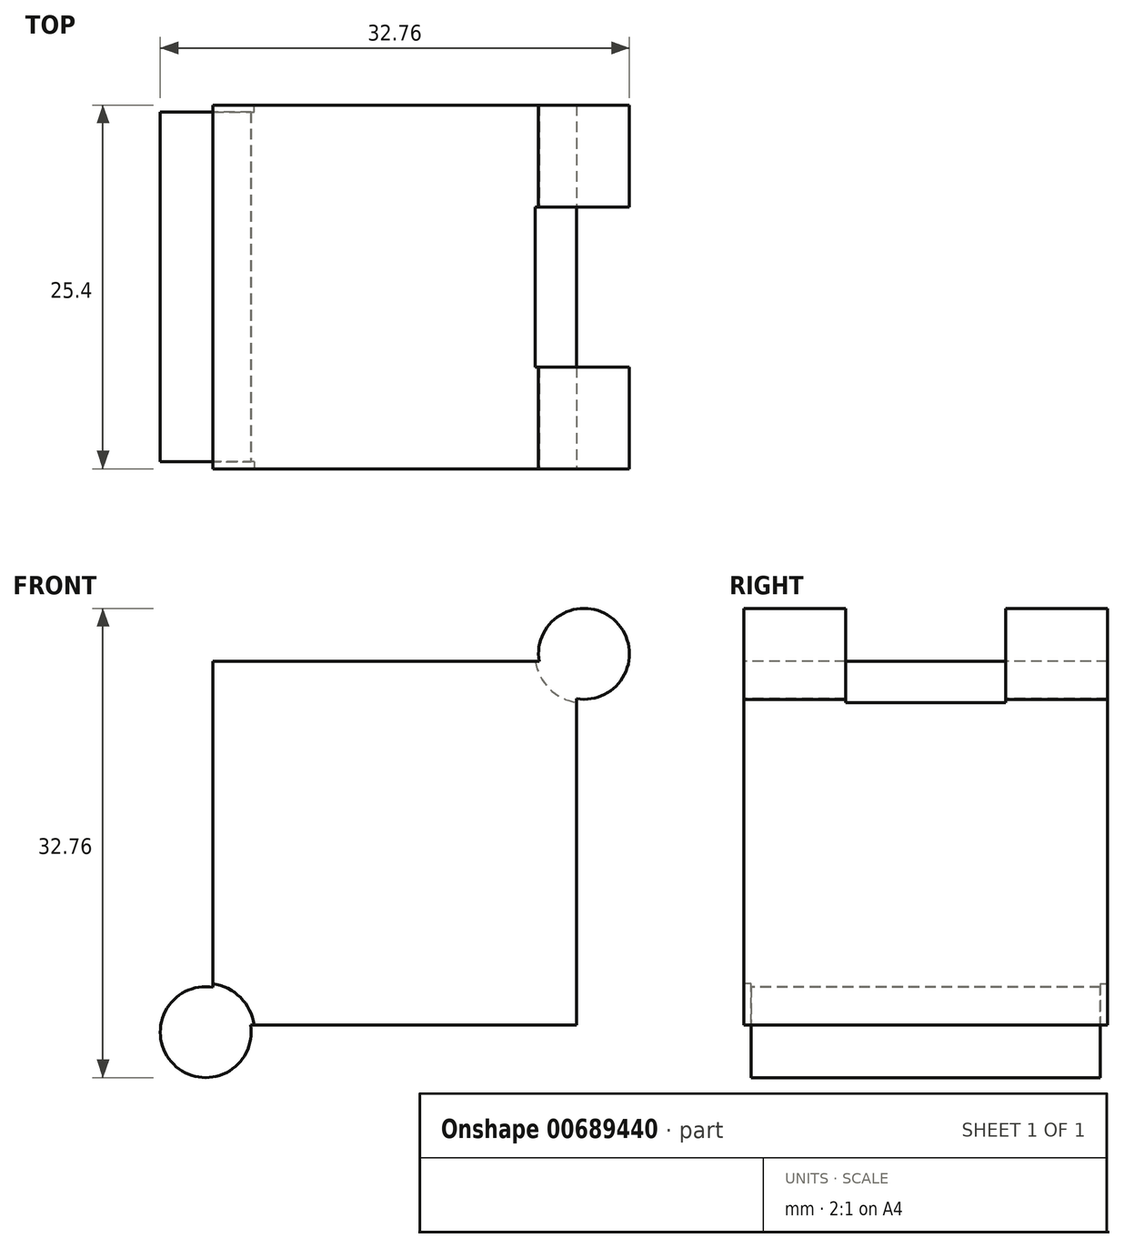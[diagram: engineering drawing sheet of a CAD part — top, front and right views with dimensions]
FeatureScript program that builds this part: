
annotation { "Feature Type Name" : "Feature", "Feature Type Description" : "" }
export const myFeature = defineFeature(function(context is Context, id is Id, definition is map)
    precondition{}
    {
        {
            assignVariable(context, id + "F0", {"name" : "O", "anyValue" : .2});
        }
        {
            var Q0;
            Q0=qCreatedBy(makeId("Front.planeOp"),FACE);
            var sketch = newSketch(context, id + "F1", { "sketchPlane" : qUnion([Q0])});
            skLineSegment(sketch, "E0.bottom", {"start": v(12.7, -12.7) * mm, "end": v(-12.7, -12.7) * mm});
            skLineSegment(sketch, "E0.top", {"start": v(12.7, 12.7) * mm, "end": v(-12.7, 12.7) * mm});
            skLineSegment(sketch, "E0.left", {"start": v(12.7, -12.7) * mm, "end": v(12.7, 12.7) * mm});
            skLineSegment(sketch, "E0.right", {"start": v(-12.7, -12.7) * mm, "end": v(-12.7, 12.7) * mm});
            skPoint(sketch, "E0.middle", {"position": v(0, 0) * mm});
            skSolve(sketch);
        }
        {
            var Q0;
            Q0=makeQuery(id+"F1.imprint","IMPRINT",FACE,{"disambiguationData":[TD([[makeQuery(id+"F1.imprint","IMPRINT",EDGE,{"derivedFrom":sQuery(id+"F1.wireOp",EDGE,"E0.bottom")}),-1.0]])]});
            extrude(context, id + "F2", {"entities" : qUnion([Q0]), "depth" : 25.4 * mm, "offsetDistance" : 25.4 * mm});
        }
        {
            var Q0;
            Q0=makeQuery(id+"F2.opExtrude","CAP_FACE",FACE,{"disambiguationData":[OSD([sQuery(id+"F1.wireOp",EDGE,"E0.bottom"),sQuery(id+"F1.wireOp",EDGE,"E0.top"),sQuery(id+"F1.wireOp",EDGE,"E0.left"),sQuery(id+"F1.wireOp",EDGE,"E0.right")])],"isStart":false});
            var sketch = newSketch(context, id + "F3", { "sketchPlane" : qUnion([Q0])});
            skCircle(sketch, "E1", {"center": v(13.2, 13.2) * mm, "radius": 3.18 * mm});
            skSolve(sketch);
        }
        {
            var Q0;
            {var subQ0=sQuery(id+"F3.wireOp",EDGE,"E1");var subQ1=makeQuery(id+"F2.opExtrude","CAP_EDGE",EDGE,{"disambiguationData":[OSD([sQuery(id+"F1.wireOp",EDGE,"E0.top")])],"isStart":false});var subQ2=makeQuery(id+"F3.imprint","INTERSECT",VERTEX,{"derivedFrom":[subQ1,subQ0]});Q0=makeQuery(id+"F3.imprint","IMPRINT",FACE,{"disambiguationData":[TD([[makeQuery(id+"F3.imprint","IMPRINT",EDGE,{"disambiguationData":[TD([[subQ2,1.0]])],"derivedFrom":subQ0}),1.0]])]});}
            var Q1;
            Q1=makeQuery(id+"F2.opExtrude","CAP_FACE",FACE,{"disambiguationData":[OSD([sQuery(id+"F1.wireOp",EDGE,"E0.bottom"),sQuery(id+"F1.wireOp",EDGE,"E0.top"),sQuery(id+"F1.wireOp",EDGE,"E0.left"),sQuery(id+"F1.wireOp",EDGE,"E0.right")])],"isStart":true});
            extrude(context, id + "F4", {"entities" : qUnion([Q0]), "operationType" : NewBodyOperationType.ADD, "endBound" : BoundingType.UP_TO_SURFACE, "oppositeDirection" : true, "depth" : 25.4 * mm, "endBoundEntityFace" : qUnion([Q1]), "offsetDistance" : 25.4 * mm});
        }
        {
            var Q0;
            {var subQ0=sQuery(id+"F1.wireOp",EDGE,"E0.left");Q0=makeQuery(id+"Fs0qjrKRxYJa69d_1.boolean.opBoolean","MERGE",FACE,{"derivedFrom":[makeQuery(id+"F2.opExtrude","SWEPT_FACE",FACE,{"disambiguationData":[OSD([subQ0])]}),makeQuery(id+"Fs0qjrKRxYJa69d_1.opExtrude","CAP_FACE",FACE,{"disambiguationData":[OSD([subQ0])],"isStart":false})]});}
            var sketch = newSketch(context, id + "F5", { "sketchPlane" : qUnion([Q0])});
            skLineSegment(sketch, "E2.bottom", {"start": v(-7.11, 4.13) * mm, "end": v(-18.29, 4.13) * mm});
            skLineSegment(sketch, "E2.top", {"start": v(-7.11, 21.77) * mm, "end": v(-18.29, 21.77) * mm});
            skLineSegment(sketch, "E2.left", {"start": v(-7.11, 4.13) * mm, "end": v(-7.11, 21.77) * mm});
            skLineSegment(sketch, "E2.right", {"start": v(-18.29, 4.13) * mm, "end": v(-18.29, 21.77) * mm});
            skPoint(sketch, "E2.middle", {"position": v(-12.7, 12.95) * mm});
            skSolve(sketch);
        }
        {
            var Q0;
            {var subQ0=sQuery(id+"F5.wireOp",EDGE,"E2.top");Q0=makeQuery(id+"F5.imprint","IMPRINT",FACE,{"disambiguationData":[TD([[makeQuery(id+"F5.imprint","IMPRINT",EDGE,{"derivedFrom":subQ0}),1.0]])]});}
            var Q1;
            {var subQ0=sQuery(id+"F5.wireOp",EDGE,"E2.bottom");Q1=makeQuery(id+"F5.imprint","IMPRINT",FACE,{"disambiguationData":[TD([[makeQuery(id+"F5.imprint","IMPRINT",EDGE,{"derivedFrom":subQ0}),-1.0]])]});}
            extrude(context, id + "F6", {"entities" : qUnion([Q0, Q1]), "operationType" : NewBodyOperationType.REMOVE, "depth" : 25.4 * mm, "offsetDistance" : 25.4 * mm});
        }
        {
            var Q0;
            Q0=makeQuery(id+"F6.boolean.opBoolean","COPY",FACE,{"derivedFrom":makeQuery(id+"F6.opExtrude","SWEPT_FACE",FACE,{"disambiguationData":[OSD([sQuery(id+"F5.wireOp",EDGE,"E2.left")])]})});
            var sketch = newSketch(context, id + "F7", { "sketchPlane" : qUnion([Q0])});
            skCircle(sketch, "E3", {"center": v(13.2, 13.2) * mm, "radius": 3.43 * mm});
            skSolve(sketch);
        }
        {
            var Q0;
            Q0=makeQuery(id+"F7.imprint","IMPRINT",FACE,{"disambiguationData":[TD([[makeQuery(id+"F7.imprint","IMPRINT",EDGE,{"derivedFrom":sQuery(id+"F7.wireOp",EDGE,"E3")}),1.0]])]});
            var Q1;
            Q1=makeQuery(id+"F6.boolean.opBoolean","COPY",FACE,{"derivedFrom":makeQuery(id+"F6.opExtrude","SWEPT_FACE",FACE,{"disambiguationData":[OSD([sQuery(id+"F5.wireOp",EDGE,"E2.right")])]})});
            extrude(context, id + "F8", {"entities" : qUnion([Q0]), "operationType" : NewBodyOperationType.REMOVE, "endBound" : BoundingType.UP_TO_SURFACE, "depth" : 25.4 * mm, "endBoundEntityFace" : qUnion([Q1]), "offsetDistance" : 25.4 * mm});
        }
        {
            var Q0;
            {var subQ0=sQuery(id+"F1.wireOp",EDGE,"E0.left");var subQ1=sQuery(id+"F1.wireOp",EDGE,"E0.top");Q0=makeQuery(id+"F4.boolean.opBoolean","MERGE",FACE,{"derivedFrom":[makeQuery(id+"F2.opExtrude","CAP_FACE",FACE,{"disambiguationData":[OSD([sQuery(id+"F1.wireOp",EDGE,"E0.bottom"),subQ1,subQ0,sQuery(id+"F1.wireOp",EDGE,"E0.right")])],"isStart":false}),makeQuery(id+"F4.opExtrude","CAP_FACE",FACE,{"disambiguationData":[OSD([subQ1,subQ0,sQuery(id+"F3.wireOp",EDGE,"E1")])],"isStart":true})]});}
            var sketch = newSketch(context, id + "F9", { "sketchPlane" : qUnion([Q0])});
            skCircle(sketch, "E4", {"center": v(-13.2, -13.2) * mm, "radius": 3.18 * mm});
            skSolve(sketch);
        }
        {
            var Q0;
            {var subQ0=sQuery(id+"F9.wireOp",EDGE,"E4");var subQ1=makeQuery(id+"F2.opExtrude","CAP_EDGE",EDGE,{"disambiguationData":[OSD([sQuery(id+"F1.wireOp",EDGE,"E0.bottom")])],"isStart":false});var subQ2=makeQuery(id+"F9.imprint","INTERSECT",VERTEX,{"derivedFrom":[subQ1,subQ0]});Q0=makeQuery(id+"F9.imprint","IMPRINT",FACE,{"disambiguationData":[TD([[makeQuery(id+"F9.imprint","IMPRINT",EDGE,{"disambiguationData":[TD([[subQ2,1.0]])],"derivedFrom":subQ0}),1.0]])]});}
            var Q1;
            {var subQ0=sQuery(id+"F1.wireOp",EDGE,"E0.right");var subQ1=sQuery(id+"F1.wireOp",EDGE,"E0.left");var subQ2=sQuery(id+"F1.wireOp",EDGE,"E0.top");var subQ3=sQuery(id+"F1.wireOp",EDGE,"E0.bottom");Q1=makeQuery(id+"F4.boolean.opBoolean","MERGE",FACE,{"derivedFrom":[makeQuery(id+"F2.opExtrude","CAP_FACE",FACE,{"disambiguationData":[OSD([subQ3,subQ2,subQ1,subQ0])],"isStart":true}),makeQuery(id+"F4.opExtrude","CAP_FACE",FACE,{"disambiguationData":[OSD([subQ3,subQ2,subQ1,subQ0])],"isStart":false})]});}
            extrude(context, id + "F10", {"entities" : qUnion([Q0]), "operationType" : NewBodyOperationType.ADD, "endBound" : BoundingType.UP_TO_SURFACE, "oppositeDirection" : true, "depth" : 25.4 * mm, "endBoundEntityFace" : qUnion([Q1]), "offsetDistance" : 25.4 * mm});
        }
        {
            var Q0;
            {var subQ0=sQuery(id+"F1.wireOp",EDGE,"E0.right");var subQ1=sQuery(id+"F1.wireOp",EDGE,"E0.bottom");var subQ2=sQuery(id+"F1.wireOp",EDGE,"E0.left");var subQ3=sQuery(id+"F1.wireOp",EDGE,"E0.top");Q0=makeQuery(id+"F10.boolean.opBoolean","MERGE",FACE,{"derivedFrom":[makeQuery(id+"F4.boolean.opBoolean","MERGE",FACE,{"derivedFrom":[makeQuery(id+"F2.opExtrude","CAP_FACE",FACE,{"disambiguationData":[OSD([subQ1,subQ3,subQ2,subQ0])],"isStart":false}),makeQuery(id+"F4.opExtrude","CAP_FACE",FACE,{"disambiguationData":[OSD([subQ3,subQ2,sQuery(id+"F3.wireOp",EDGE,"E1")])],"isStart":true})]}),makeQuery(id+"F10.opExtrude","CAP_FACE",FACE,{"disambiguationData":[OSD([subQ1,subQ0,sQuery(id+"F9.wireOp",EDGE,"E4")])],"isStart":true})]});}
            var sketch = newSketch(context, id + "F11", { "sketchPlane" : qUnion([Q0])});
            skCircle(sketch, "E5", {"center": v(-13.2, -13.2) * mm, "radius": 3.43 * mm});
            skSolve(sketch);
        }
        {
            var Q0;
            {var subQ0=sQuery(id+"F1.wireOp",EDGE,"E0.right");var subQ1=sQuery(id+"F1.wireOp",EDGE,"E0.left");var subQ2=sQuery(id+"F1.wireOp",EDGE,"E0.top");var subQ3=sQuery(id+"F1.wireOp",EDGE,"E0.bottom");Q0=makeQuery(id+"F10.boolean.opBoolean","MERGE",FACE,{"derivedFrom":[makeQuery(id+"F4.boolean.opBoolean","MERGE",FACE,{"derivedFrom":[makeQuery(id+"F2.opExtrude","CAP_FACE",FACE,{"disambiguationData":[OSD([subQ3,subQ2,subQ1,subQ0])],"isStart":true}),makeQuery(id+"F4.opExtrude","CAP_FACE",FACE,{"disambiguationData":[OSD([subQ3,subQ2,subQ1,subQ0])],"isStart":false})]}),makeQuery(id+"F10.opExtrude","CAP_FACE",FACE,{"disambiguationData":[OSD([subQ3,subQ2,subQ1,subQ0])],"isStart":false})]});}
            var sketch = newSketch(context, id + "F12", { "sketchPlane" : qUnion([Q0])});
            skCircle(sketch, "E6", {"center": v(13.2, -13.2) * mm, "radius": 3.43 * mm});
            skSolve(sketch);
        }
        {
            var Q0;
            {var subQ0=sQuery(id+"F12.wireOp",EDGE,"E6");var subQ1=sQuery(id+"F1.wireOp",EDGE,"E0.bottom");var subQ2=makeQuery(id+"F2.opExtrude","CAP_EDGE",EDGE,{"disambiguationData":[OSD([subQ1])],"isStart":true});var subQ3=makeQuery(id+"F12.imprint","INTERSECT",VERTEX,{"derivedFrom":[subQ2,subQ0]});Q0=makeQuery(id+"F12.imprint","IMPRINT",FACE,{"disambiguationData":[TD([[makeQuery(id+"F12.imprint","IMPRINT",EDGE,{"disambiguationData":[TD([[subQ3,-1.0]])],"derivedFrom":subQ0}),1.0]])]});}
            var Q1;
            {var subQ0=sQuery(id+"F12.wireOp",EDGE,"E6");var subQ1=sQuery(id+"F1.wireOp",EDGE,"E0.bottom");var subQ2=makeQuery(id+"F2.opExtrude","CAP_EDGE",EDGE,{"disambiguationData":[OSD([subQ1])],"isStart":true});var subQ3=makeQuery(id+"F12.imprint","INTERSECT",VERTEX,{"derivedFrom":[subQ2,subQ0]});Q1=makeQuery(id+"F12.imprint","IMPRINT",FACE,{"disambiguationData":[TD([[makeQuery(id+"F12.imprint","IMPRINT",EDGE,{"disambiguationData":[TD([[subQ3,1.0]])],"derivedFrom":subQ0}),1.0]])]});}
            extrude(context, id + "F13", {"entities" : qUnion([Q0, Q1]), "operationType" : NewBodyOperationType.REMOVE, "oppositeDirection" : true, "depth" : (.3 + getVariable(context, 'O')) * mm, "offsetDistance" : 25.4 * mm});
        }
        {
            var Q0;
            {var subQ5=makeQuery(id+"F10.opExtrude","CAP_EDGE",EDGE,{"disambiguationData":[OSD([sQuery(id+"F9.wireOp",EDGE,"E4")])],"isStart":true});Q0=makeQuery(id+"F11.imprint","IMPRINT",FACE,{"disambiguationData":[TD([[makeQuery(id+"F11.imprint","IMPRINT",EDGE,{"derivedFrom":subQ5}),-1.0]])]});}
            var Q1;
            {var subQ5=makeQuery(id+"F10.opExtrude","CAP_EDGE",EDGE,{"disambiguationData":[OSD([sQuery(id+"F9.wireOp",EDGE,"E4")])],"isStart":true});Q1=makeQuery(id+"F11.imprint","IMPRINT",FACE,{"disambiguationData":[TD([[makeQuery(id+"F11.imprint","IMPRINT",EDGE,{"derivedFrom":subQ5}),1.0]])]});}
            extrude(context, id + "F14", {"entities" : qUnion([Q0, Q1]), "operationType" : NewBodyOperationType.REMOVE, "oppositeDirection" : true, "depth" : (.3 + getVariable(context, 'O')) * mm, "offsetDistance" : 25.4 * mm});
        }
    });
